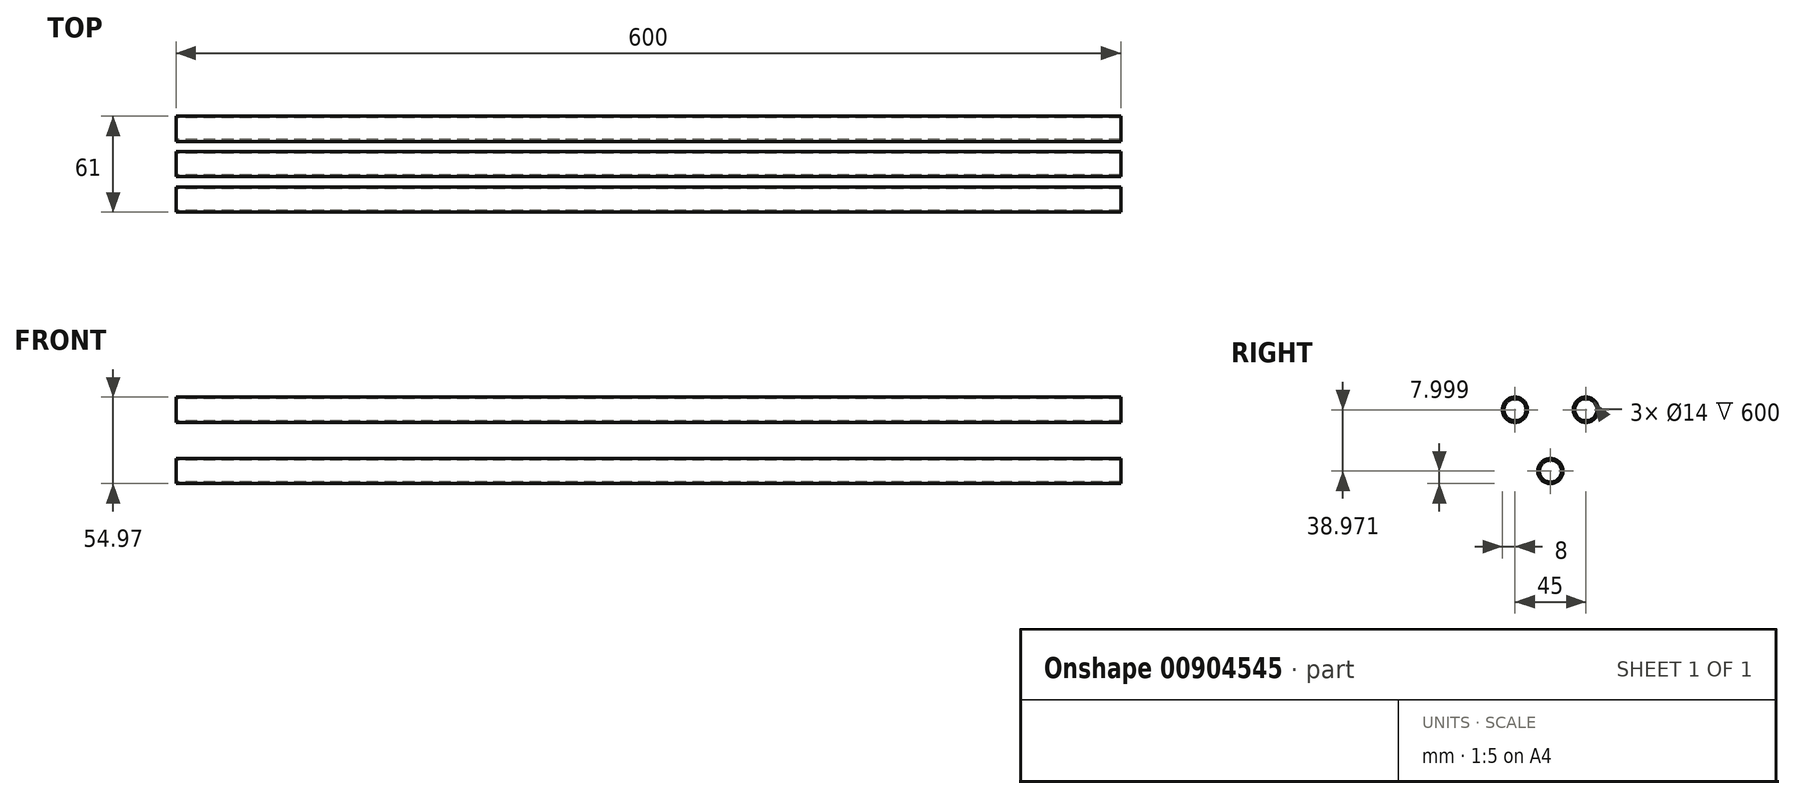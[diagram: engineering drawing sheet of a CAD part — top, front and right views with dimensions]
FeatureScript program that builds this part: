
annotation { "Feature Type Name" : "Feature", "Feature Type Description" : "" }
export const myFeature = defineFeature(function(context is Context, id is Id, definition is map)
    precondition{}
    {
        {
            var Q0;
            Q0=qCreatedBy(makeId("Right.planeOp"),FACE);
            var sketch = newSketch(context, id + "F0", { "sketchPlane" : qUnion([Q0])});
            skCircle(sketch, "E0", {"center": v(0, 0) * mm, "radius": 8 * mm});
            skCircle(sketch, "E1", {"center": v(45, 0) * mm, "radius": 8 * mm});
            skCircle(sketch, "E2", {"center": v(22.5, -38.97) * mm, "radius": 8 * mm});
            skCircle(sketch, "E3", {"center": v(0, 0) * mm, "radius": 7 * mm});
            skCircle(sketch, "E4", {"center": v(45, 0) * mm, "radius": 7 * mm});
            skCircle(sketch, "E5", {"center": v(22.5, -38.97) * mm, "radius": 7 * mm});
            skSolve(sketch);
        }
        {
            var Q0;
            Q0=makeQuery(id+"F0.imprint","IMPRINT",FACE,{"disambiguationData":[TD([[makeQuery(id+"F0.imprint","IMPRINT",EDGE,{"derivedFrom":sQuery(id+"F0.wireOp",EDGE,"E0")}),1.0]])]});
            var Q1;
            Q1=makeQuery(id+"F0.imprint","IMPRINT",FACE,{"disambiguationData":[TD([[makeQuery(id+"F0.imprint","IMPRINT",EDGE,{"derivedFrom":sQuery(id+"F0.wireOp",EDGE,"E1")}),1.0]])]});
            var Q2;
            Q2=makeQuery(id+"F0.imprint","IMPRINT",FACE,{"disambiguationData":[TD([[makeQuery(id+"F0.imprint","IMPRINT",EDGE,{"derivedFrom":sQuery(id+"F0.wireOp",EDGE,"E2")}),1.0]])]});
            extrude(context, id + "F1", {"entities" : qUnion([Q0, Q1, Q2]), "depth" : 600 * mm, "offsetDistance" : 25 * mm});
        }
    });
